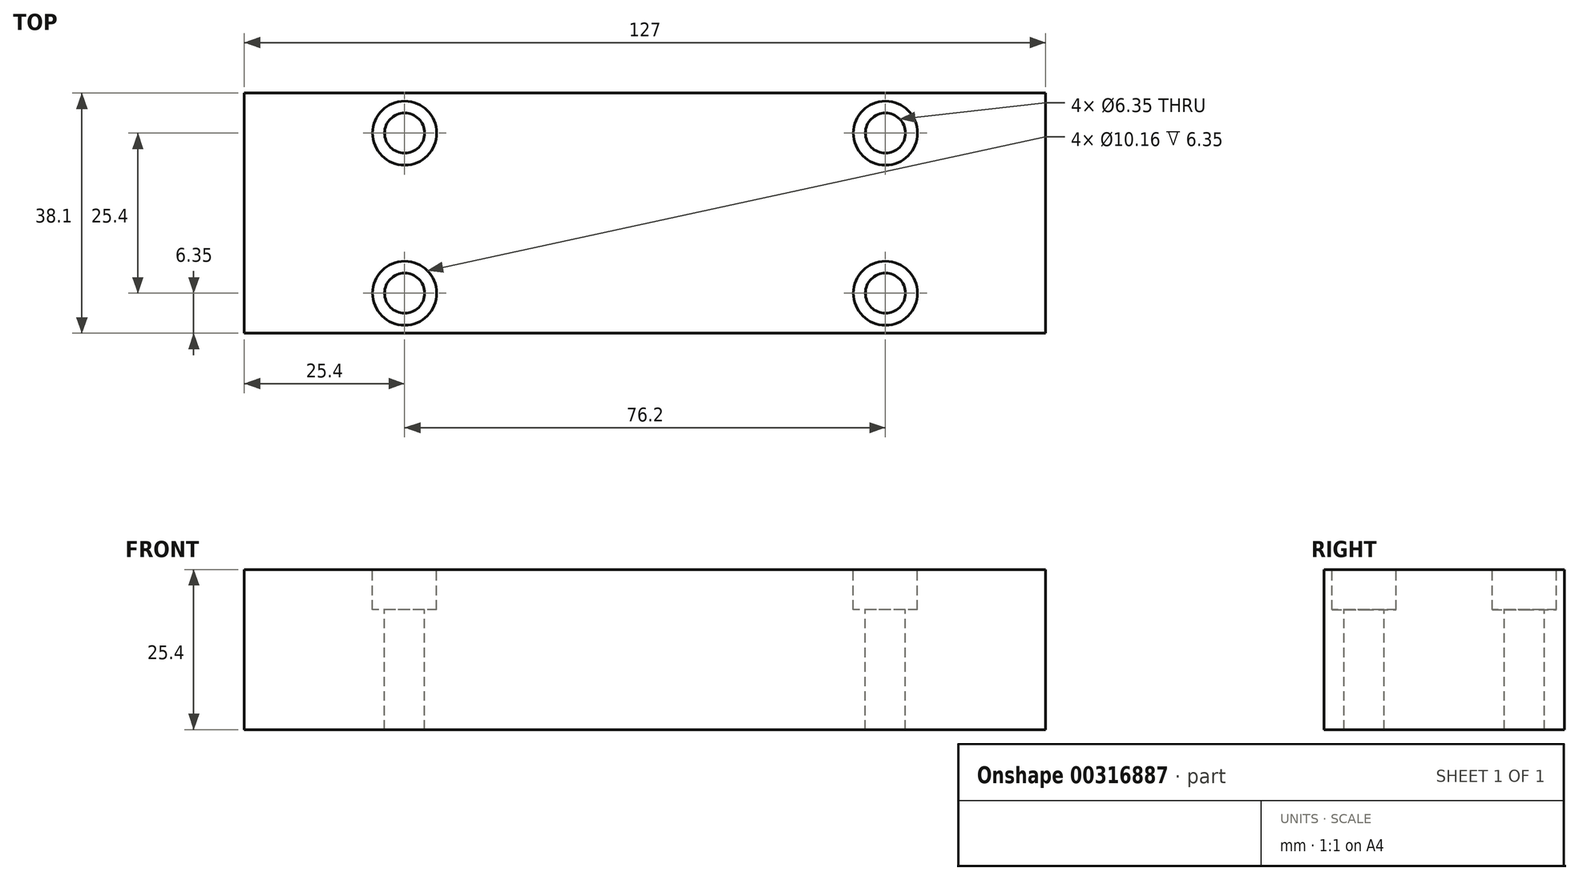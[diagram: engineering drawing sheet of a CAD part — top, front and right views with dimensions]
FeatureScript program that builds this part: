
annotation { "Feature Type Name" : "Feature", "Feature Type Description" : "" }
export const myFeature = defineFeature(function(context is Context, id is Id, definition is map)
    precondition{}
    {
        {
            var Q0;
            Q0=qCreatedBy(makeId("Top.planeOp"),FACE);
            var sketch = newSketch(context, id + "F0", { "sketchPlane" : qUnion([Q0])});
            skLineSegment(sketch, "E0.bottom", {"start": v(63.5, 19.05) * mm, "end": v(-63.5, 19.05) * mm});
            skLineSegment(sketch, "E0.top", {"start": v(63.5, -19.05) * mm, "end": v(-63.5, -19.05) * mm});
            skLineSegment(sketch, "E0.left", {"start": v(63.5, 19.05) * mm, "end": v(63.5, -19.05) * mm});
            skLineSegment(sketch, "E0.right", {"start": v(-63.5, 19.05) * mm, "end": v(-63.5, -19.05) * mm});
            skPoint(sketch, "E0.middle", {"position": v(0, 0) * mm});
            skSolve(sketch);
        }
        {
            var Q0;
            Q0=makeQuery(id+"F0.imprint","IMPRINT",FACE,{"disambiguationData":[TD([[makeQuery(id+"F0.imprint","IMPRINT",EDGE,{"derivedFrom":sQuery(id+"F0.wireOp",EDGE,"E0.bottom")}),1.0]])]});
            extrude(context, id + "F1", {"entities" : qUnion([Q0]), "depth" : 25.4 * mm});
        }
        {
            var Q0;
            Q0=makeQuery(id+"F1.opExtrude","CAP_FACE",FACE,{"disambiguationData":[OSD([sQuery(id+"F0.wireOp",EDGE,"E0.bottom"),sQuery(id+"F0.wireOp",EDGE,"E0.top"),sQuery(id+"F0.wireOp",EDGE,"E0.left"),sQuery(id+"F0.wireOp",EDGE,"E0.right")])],"isStart":false});
            var sketch = newSketch(context, id + "F2", { "sketchPlane" : qUnion([Q0])});
            skLineSegment(sketch, "E1.bottom", {"start": v(38.1, -12.7) * mm, "end": v(-38.1, -12.7) * mm});
            skLineSegment(sketch, "E1.top", {"start": v(38.1, 12.7) * mm, "end": v(-38.1, 12.7) * mm});
            skLineSegment(sketch, "E1.left", {"start": v(38.1, -12.7) * mm, "end": v(38.1, 12.7) * mm});
            skLineSegment(sketch, "E1.right", {"start": v(-38.1, -12.7) * mm, "end": v(-38.1, 12.7) * mm});
            skPoint(sketch, "E1.middle", {"position": v(0, 0) * mm});
            skSolve(sketch);
        }
        {
            var Q0;
            Q0=sQuery(id+"F2.wireOp",VERTEX,"E1.top.end");
            var Q1;
            Q1=sQuery(id+"F2.wireOp",VERTEX,"E1.right.start");
            var Q2;
            Q2=sQuery(id+"F2.wireOp",VERTEX,"E1.left.start");
            var Q3;
            Q3=sQuery(id+"F2.wireOp",VERTEX,"E1.left.end");
            var Q4;
            Q4=makeQuery(id+"F1.opExtrude","SWEPT_BODY",BODY,{"disambiguationData":[OSD([sQuery(id+"F0.wireOp",EDGE,"E0.bottom"),sQuery(id+"F0.wireOp",EDGE,"E0.top"),sQuery(id+"F0.wireOp",EDGE,"E0.left"),sQuery(id+"F0.wireOp",EDGE,"E0.right")])]});
            hole(context, id + "F3", {"style" : HoleStyle.C_BORE, "endStyle" : HoleEndStyle.THROUGH, "holeDiameter" : 6.35 * mm, "cBoreDiameter" : 10.16 * mm, "cBoreDepth" : 6.35 * mm, "tappedDepth" : 12.7 * mm, "tapClearance" : 3, "locations" : qUnion([Q0, Q1, Q2, Q3]), "scope" : qUnion([Q4])});
        }
    });
